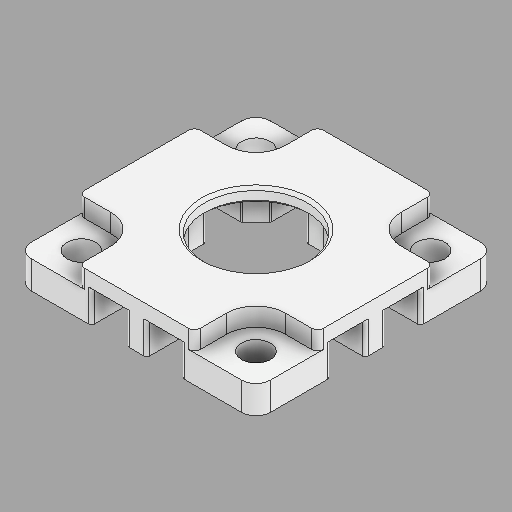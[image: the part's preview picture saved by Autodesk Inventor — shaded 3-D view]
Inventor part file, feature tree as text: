
AUTODESK INVENTOR PART (.ipt)
format: ipt  version: 2024.2 (Build 282272000, 272)  size: 196,096 bytes
history: native  units: in
note: dims shown in document units (in); Inventor stores cm internally (conversion verified against a paired STEP export)
features: fillet x1
ambient origin geometry x8: Origin, YZ Plane, XZ Plane, XY Plane, X Axis, Y Axis, Z Axis, Center Point
bodies: Solid1 (feature_tree)
feature tree (1):
  fillet  "Fillet4"  [1 undecoded]
note: 1 required parameter value undecoded (feature->parameter linkage not recoverable at this tier; creation-order binding heuristic only, values carry confidence <= 0.55)
